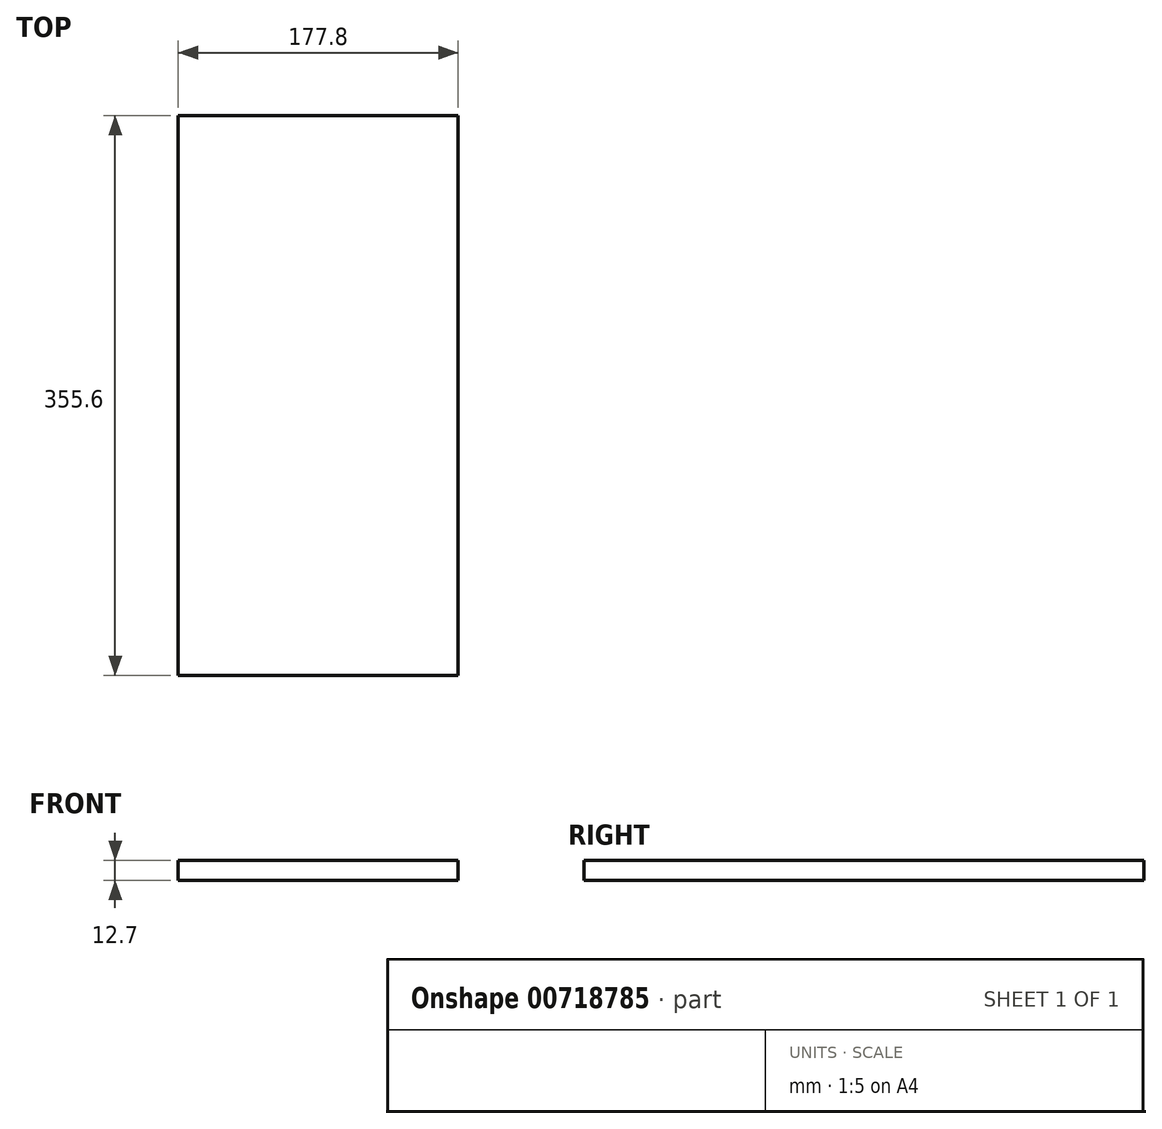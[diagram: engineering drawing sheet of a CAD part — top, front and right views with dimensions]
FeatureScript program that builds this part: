
annotation { "Feature Type Name" : "Feature", "Feature Type Description" : "" }
export const myFeature = defineFeature(function(context is Context, id is Id, definition is map)
    precondition{}
    {
        {
            var Q0;
            Q0=qCreatedBy(makeId("Top.planeOp"),FACE);
            var sketch = newSketch(context, id + "F0", { "sketchPlane" : qUnion([Q0])});
            skLineSegment(sketch, "E0.bottom", {"start": v(-87.25, 238.13) * mm, "end": v(90.55, 238.13) * mm});
            skLineSegment(sketch, "E0.top", {"start": v(-87.25, -117.47) * mm, "end": v(90.55, -117.47) * mm});
            skLineSegment(sketch, "E0.left", {"start": v(-87.25, 238.13) * mm, "end": v(-87.25, -117.47) * mm});
            skLineSegment(sketch, "E0.right", {"start": v(90.55, 238.13) * mm, "end": v(90.55, -117.47) * mm});
            skSolve(sketch);
        }
        {
            var Q0;
            Q0=makeQuery(id+"F0.imprint","IMPRINT",FACE,{"disambiguationData":[TD([[makeQuery(id+"F0.imprint","IMPRINT",EDGE,{"derivedFrom":sQuery(id+"F0.wireOp",EDGE,"E0.bottom")}),-1.0]])]});
            extrude(context, id + "F1", {"entities" : qUnion([Q0]), "depth" : 12.7 * mm, "offsetDistance" : 25.4 * mm});
        }
    });
